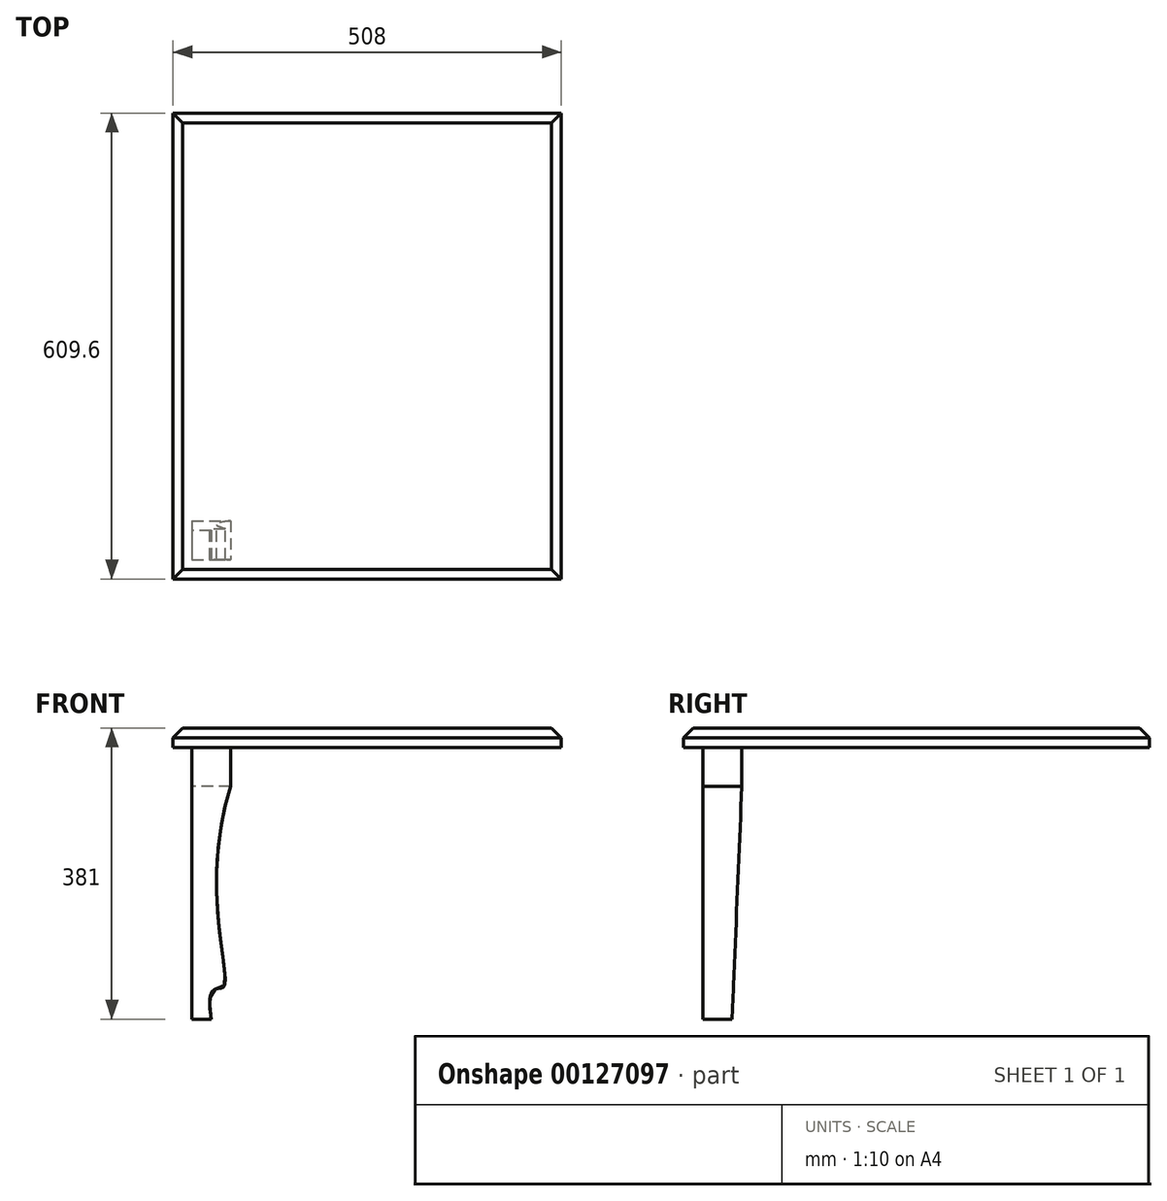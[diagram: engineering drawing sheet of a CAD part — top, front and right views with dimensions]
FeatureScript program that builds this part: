
annotation { "Feature Type Name" : "Feature", "Feature Type Description" : "" }
export const myFeature = defineFeature(function(context is Context, id is Id, definition is map)
    precondition{}
    {
        {
            var Q0;
            Q0=qCreatedBy(makeId("Top.planeOp"),FACE);
            var sketch = newSketch(context, id + "F0", { "sketchPlane" : qUnion([Q0])});
            skLineSegment(sketch, "E0.bottom", {"start": v(-455.57, 346.85) * mm, "end": v(52.43, 346.85) * mm});
            skLineSegment(sketch, "E0.top", {"start": v(-455.57, -262.75) * mm, "end": v(52.43, -262.75) * mm});
            skLineSegment(sketch, "E0.left", {"start": v(-455.57, 346.85) * mm, "end": v(-455.57, -262.75) * mm});
            skLineSegment(sketch, "E0.right", {"start": v(52.43, 346.85) * mm, "end": v(52.43, -262.75) * mm});
            skSolve(sketch);
        }
        {
            var Q0;
            Q0=makeQuery(id+"F0.imprint","IMPRINT",FACE,{"disambiguationData":[TD([[makeQuery(id+"F0.imprint","IMPRINT",EDGE,{"derivedFrom":sQuery(id+"F0.wireOp",EDGE,"E0.bottom")}),-1.0]])]});
            extrude(context, id + "F1", {"entities" : qUnion([Q0]), "oppositeDirection" : true, "depth" : 25.4 * mm});
        }
        {
            var Q0;
            Q0=makeQuery(id+"F1.opExtrude","CAP_EDGE",EDGE,{"disambiguationData":[OSD([sQuery(id+"F0.wireOp",EDGE,"E0.top")])],"isStart":true});
            var Q1;
            Q1=makeQuery(id+"F1.opExtrude","CAP_EDGE",EDGE,{"disambiguationData":[OSD([sQuery(id+"F0.wireOp",EDGE,"E0.right")])],"isStart":true});
            var Q2;
            Q2=makeQuery(id+"F1.opExtrude","CAP_EDGE",EDGE,{"disambiguationData":[OSD([sQuery(id+"F0.wireOp",EDGE,"E0.bottom")])],"isStart":true});
            var Q3;
            Q3=makeQuery(id+"F1.opExtrude","CAP_EDGE",EDGE,{"disambiguationData":[OSD([sQuery(id+"F0.wireOp",EDGE,"E0.left")])],"isStart":true});
            chamfer(context, id + "F2", {"entities" : qUnion([Q0, Q1, Q2, Q3]), "width" : 12.7 * mm, "tangentPropagation" : true});
        }
        {
            var Q0;
            Q0=makeQuery(id+"F1.opExtrude","SWEPT_FACE",FACE,{"disambiguationData":[OSD([sQuery(id+"F0.wireOp",EDGE,"E0.top")])]});
            cPlane(context, id + "F3", {"entities" : qUnion([Q0]), "cplaneType" : CPlaneType.OFFSET, "offset" : 25.4 * mm, "oppositeDirection" : true, "width" : 152.4 * mm, "height" : 152.4 * mm});
        }
        {
            var Q0;
            Q0=qCreatedBy(id+"F3.planeOp",FACE);
            var sketch = newSketch(context, id + "F4", { "sketchPlane" : qUnion([Q0])});
            skLineSegment(sketch, "E1.0", {"start": v(-442.87, 0) * mm, "end": v(39.73, 0) * mm});
            skLineSegment(sketch, "E2", {"start": v(-431, 0) * mm, "end": v(-431, -381) * mm});
            skLineSegment(sketch, "E3", {"start": v(-380.2, 0) * mm, "end": v(-380.2, -76.2) * mm});
            skLineSegment(sketch, "E4", {"start": v(-431, -381) * mm, "end": v(-405.6, -381) * mm});
            skFitSpline(sketch, "E5", {"points": [v(-380.2, -76.2) * mm, v(-390.5, -339.96) * mm, v(-405.6, -381) * mm], "startDerivative": vector(-181.5, -587.5) * mm, "endDerivative": vector(81.39, -516.1) * mm});
            skSolve(sketch);
        }
        {
            var Q0;
            {var subQ1=sQuery(id+"F4.wireOp",EDGE,"E2");Q0=makeQuery(id+"F4.imprint","IMPRINT",FACE,{"disambiguationData":[TD([[makeQuery(id+"F4.imprint","IMPRINT",EDGE,{"derivedFrom":subQ1}),1.0]])]});}
            extrude(context, id + "F5", {"entities" : qUnion([Q0]), "operationType" : NewBodyOperationType.ADD, "oppositeDirection" : true, "depth" : 50.8 * mm});
        }
        {
            var Q0;
            Q0=makeQuery(id+"F5.opExtrude","SWEPT_FACE",FACE,{"disambiguationData":[OSD([sQuery(id+"F4.wireOp",EDGE,"E2")])]});
            var sketch = newSketch(context, id + "F6", { "sketchPlane" : qUnion([Q0])});
            skLineSegment(sketch, "E6.0", {"start": v(186.55, 0) * mm, "end": v(186.55, -381) * mm});
            skLineSegment(sketch, "E7.0", {"start": v(186.55, -381) * mm, "end": v(237.35, -381) * mm});
            skLineSegment(sketch, "E8", {"start": v(186.55, -76.14) * mm, "end": v(199.25, -381) * mm});
            skSolve(sketch);
        }
        {
            var Q0;
            {var subQ3=sQuery(id+"F6.wireOp",EDGE,"E8");Q0=makeQuery(id+"F6.imprint","IMPRINT",FACE,{"disambiguationData":[TD([[makeQuery(id+"F6.imprint","IMPRINT",EDGE,{"derivedFrom":subQ3}),-1.0]])]});}
            extrude(context, id + "F7", {"entities" : qUnion([Q0]), "operationType" : NewBodyOperationType.REMOVE, "oppositeDirection" : true, "depth" : 100.2 * mm});
        }
        {
            var Q0;
            Q0=makeQuery(id+"F1.opExtrude","SWEPT_FACE",FACE,{"disambiguationData":[OSD([sQuery(id+"F0.wireOp",EDGE,"E0.top")])]});
            var Q1;
            Q1=makeQuery(id+"F1.opExtrude","SWEPT_FACE",FACE,{"disambiguationData":[OSD([sQuery(id+"F0.wireOp",EDGE,"E0.bottom")])]});
            cPlane(context, id + "F8", {"entities" : qUnion([Q0, Q1]), "cplaneType" : CPlaneType.MID_PLANE, "offset" : 25.4 * mm, "width" : 152.4 * mm, "height" : 152.4 * mm});
        }
        {
            var Q0;
            Q0=makeQuery(id+"F1.opExtrude","SWEPT_FACE",FACE,{"disambiguationData":[OSD([sQuery(id+"F0.wireOp",EDGE,"E0.left")])]});
            var Q1;
            Q1=makeQuery(id+"F1.opExtrude","SWEPT_FACE",FACE,{"disambiguationData":[OSD([sQuery(id+"F0.wireOp",EDGE,"E0.right")])]});
            cPlane(context, id + "F9", {"entities" : qUnion([Q0, Q1]), "cplaneType" : CPlaneType.MID_PLANE, "offset" : 25.4 * mm, "width" : 152.4 * mm, "height" : 152.4 * mm});
        }
    });
